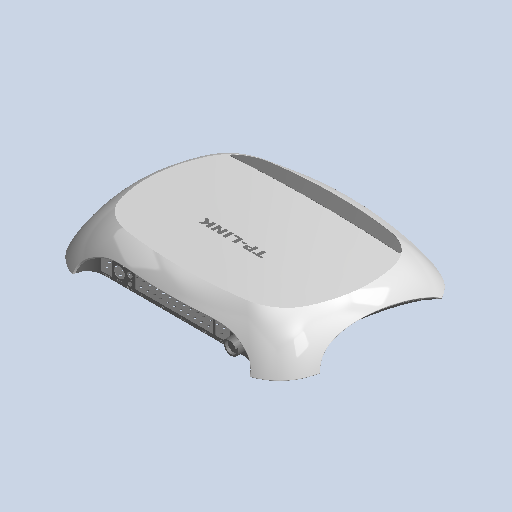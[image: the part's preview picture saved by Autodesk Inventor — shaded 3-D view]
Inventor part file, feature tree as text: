
AUTODESK INVENTOR PART (.ipt)
format: ipt  version: 2022.1 (Build 261234000, 234)  size: 7,215,104 bytes
history: mixed  units: mm (DEFAULTED — no unit token found)
features: other x10, fillet x2, chamfer x1, imported_body x1
bodies: Body1 (imported_parasolid), Body2 (imported_parasolid), Body3 (imported_parasolid)
feature tree (14):
  other  "Sólido1"
  other  "Origen"
  other  "Plano YZ"
  other  "Plano XZ"
  other  "Plano XY"
  other  "Eje X"
  other  "Eje Y"
  other  "Eje Z"
  other  "Sólido2"
  other  "Sólido3"
  fillet  "Fillet4"  [1 undecoded]
  fillet  "Fillet11"  [1 undecoded]
  chamfer  "Chamfer1"  [1 undecoded]
  imported_body  NMx_Import_Brep_tag  [imported B-rep: ~6 faces, bbox_mm=None]
note: 3 required parameter values undecoded (feature->parameter linkage not recoverable at this tier; creation-order binding heuristic only, values carry confidence <= 0.55)
